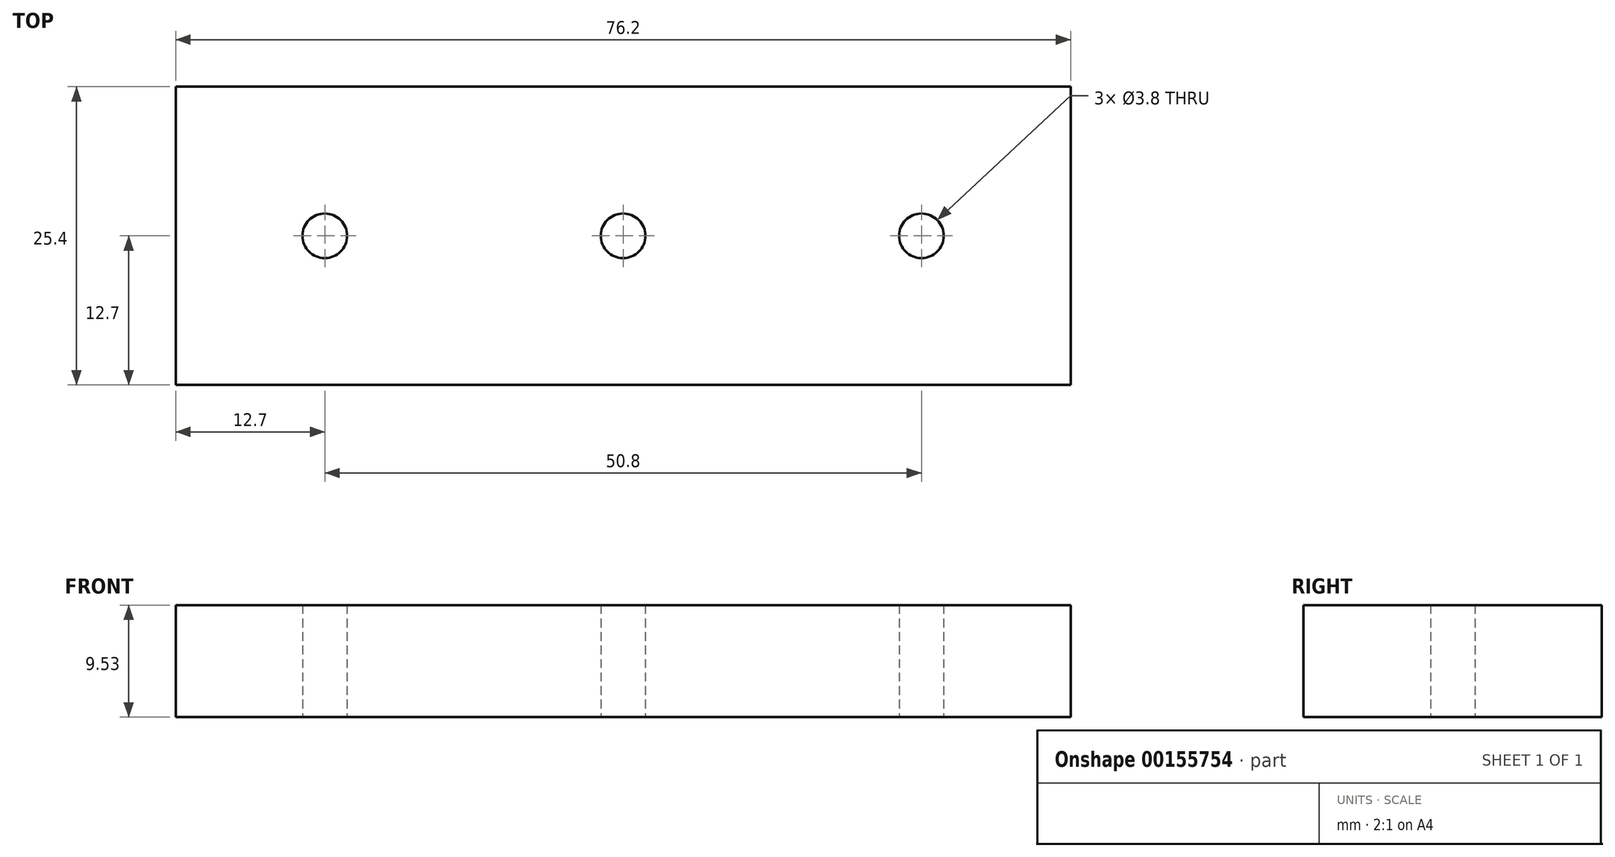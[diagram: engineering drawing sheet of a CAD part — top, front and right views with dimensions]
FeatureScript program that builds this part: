
annotation { "Feature Type Name" : "Feature", "Feature Type Description" : "" }
export const myFeature = defineFeature(function(context is Context, id is Id, definition is map)
    precondition{}
    {
        {
            var Q0;
            Q0=qCreatedBy(makeId("Top.planeOp"),FACE);
            var sketch = newSketch(context, id + "F0", { "sketchPlane" : qUnion([Q0])});
            skLineSegment(sketch, "E0.bottom", {"start": v(-38.1, 12.7) * mm, "end": v(38.1, 12.7) * mm});
            skLineSegment(sketch, "E0.top", {"start": v(-38.1, -12.7) * mm, "end": v(38.1, -12.7) * mm});
            skLineSegment(sketch, "E0.left", {"start": v(-38.1, 12.7) * mm, "end": v(-38.1, -12.7) * mm});
            skLineSegment(sketch, "E0.right", {"start": v(38.1, 12.7) * mm, "end": v(38.1, -12.7) * mm});
            skPoint(sketch, "E0.middle", {"position": v(0, 0) * mm});
            skLineSegment(sketch, "E1", {"start": v(0, 40.4) * mm, "end": v(0, -26.04) * mm, "construction": true});
            skPoint(sketch, "E2", {"position": v(-25.4, 0) * mm});
            skPoint(sketch, "E3", {"position": v(25.4, 0) * mm});
            skSolve(sketch);
        }
        {
            var Q0;
            Q0 = qSketchRegion(id + "F0", true);
            extrude(context, id + "F1", {"entities" : qUnion([Q0]), "oppositeDirection" : true, "depth" : .375 * 25.4 * mm});
        }
        {
            var Q0;
            Q0=sQuery(id+"F0.wireOp",VERTEX,"E2");
            var Q1;
            Q1=sQuery(id+"F0.wireOp",VERTEX,"E3");
            var Q2;
            Q2=sQuery(id+"F0.wireOp",VERTEX,"E0.middle");
            var Q3;
            Q3=makeQuery(id+"F1.opExtrude","SWEPT_BODY",BODY,{"disambiguationData":[OSD([sQuery(id+"F0.wireOp",EDGE,"E0.bottom"),sQuery(id+"F0.wireOp",EDGE,"E0.top"),sQuery(id+"F0.wireOp",EDGE,"E0.left"),sQuery(id+"F0.wireOp",EDGE,"E0.right")])]});
            hole(context, id + "F2", {"style" : HoleStyle.SIMPLE, "endStyle" : HoleEndStyle.THROUGH, "standardTappedOrClearance" : lookupTablePath({ "standard" : "ANSI", "engagement" : "75%", "pitch" : "24 tpi", "size" : "#10", "type" : "Tapped" }), "standardBlindInLast" : lookupTablePath({ "standard" : "ANSI", "engagement" : "75%", "pitch" : "24 tpi", "size" : "#10", "type" : "Tapped" }), "holeDiameter" : 3.8 * mm, "showTappedDepth" : true, "tappedDepth" : 12 * mm, "tapClearance" : 3, "locations" : qUnion([Q0, Q1, Q2]), "scope" : qUnion([Q3]), "majorDiameter" : 4.83 * mm});
        }
    });
